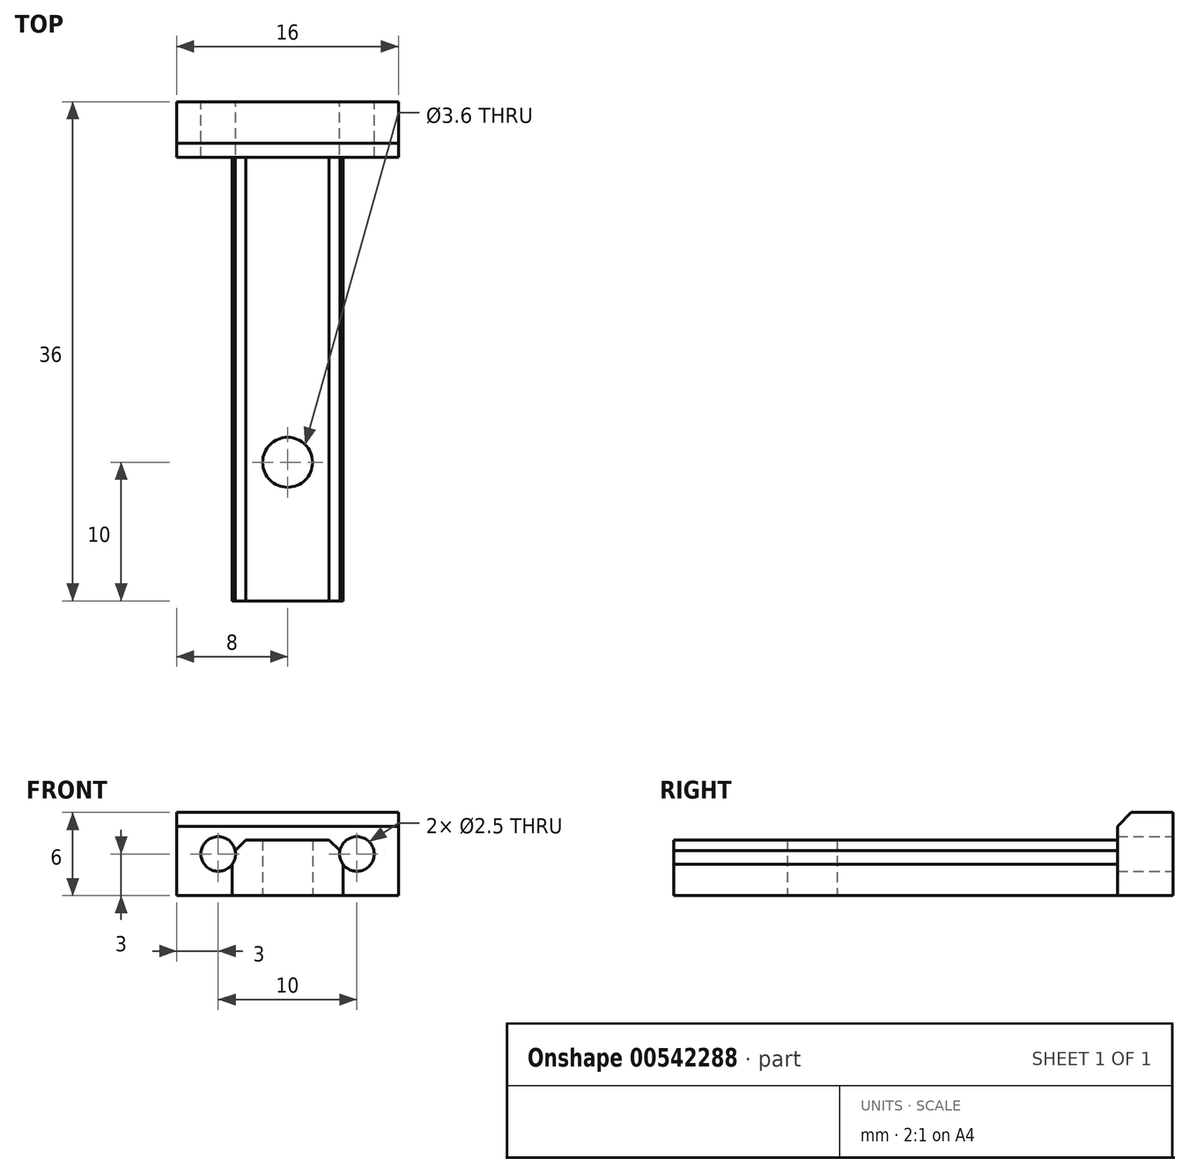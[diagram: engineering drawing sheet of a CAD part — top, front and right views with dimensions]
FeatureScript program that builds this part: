
annotation { "Feature Type Name" : "Feature", "Feature Type Description" : "" }
export const myFeature = defineFeature(function(context is Context, id is Id, definition is map)
    precondition{}
    {
        {
            var Q0;
            Q0=qCreatedBy(makeId("Top.planeOp"),FACE);
            var sketch = newSketch(context, id + "F0", { "sketchPlane" : qUnion([Q0])});
            skLineSegment(sketch, "E0", {"start": v(0, 0) * mm, "end": v(0, 26) * mm, "construction": true});
            skLineSegment(sketch, "E1", {"start": v(0, 0) * mm, "end": v(0, -10) * mm, "construction": true});
            skLineSegment(sketch, "E2", {"start": v(0, 26) * mm, "end": v(-8, 26) * mm});
            skLineSegment(sketch, "E3", {"start": v(0, 26) * mm, "end": v(8, 26) * mm});
            skLineSegment(sketch, "E4", {"start": v(-8, 26) * mm, "end": v(-8, 22) * mm});
            skLineSegment(sketch, "E5", {"start": v(-8, 22) * mm, "end": v(-4, 22) * mm});
            skLineSegment(sketch, "E6", {"start": v(8, 26) * mm, "end": v(8, 22) * mm});
            skLineSegment(sketch, "E7", {"start": v(8, 22) * mm, "end": v(4, 22) * mm});
            skLineSegment(sketch, "E8", {"start": v(0, -10) * mm, "end": v(-4, -10) * mm});
            skLineSegment(sketch, "E9", {"start": v(0, -10) * mm, "end": v(4, -10) * mm});
            skLineSegment(sketch, "E10", {"start": v(-4, 22) * mm, "end": v(-4, -10) * mm});
            skLineSegment(sketch, "E11", {"start": v(4, -10) * mm, "end": v(4, 22) * mm});
            skCircle(sketch, "E12", {"center": v(0, 0) * mm, "radius": 1.8 * mm});
            skLineSegment(sketch, "E13", {"start": v(-4, 22) * mm, "end": v(4, 22) * mm});
            skSolve(sketch);
        }
        {
            var Q0;
            Q0=makeQuery(id+"F0.imprint","IMPRINT",FACE,{"disambiguationData":[TD([[makeQuery(id+"F0.imprint","IMPRINT",EDGE,{"derivedFrom":sQuery(id+"F0.wireOp",EDGE,"E8")}),-1.0]])]});
            extrude(context, id + "F1", {"entities" : qUnion([Q0]), "depth" : 4 * mm, "offsetDistance" : 25 * mm});
        }
        {
            var Q0;
            Q0=makeQuery(id+"F0.imprint","IMPRINT",FACE,{"disambiguationData":[TD([[makeQuery(id+"F0.imprint","IMPRINT",EDGE,{"derivedFrom":sQuery(id+"F0.wireOp",EDGE,"E2")}),1.0]])]});
            extrude(context, id + "F2", {"entities" : qUnion([Q0]), "operationType" : NewBodyOperationType.ADD, "depth" : 6 * mm, "offsetDistance" : 25 * mm});
        }
        {
            var Q0;
            Q0=makeQuery(id+"F2.opExtrude","SWEPT_FACE",FACE,{"disambiguationData":[OSD([sQuery(id+"F0.wireOp",EDGE,"E2"),sQuery(id+"F0.wireOp",EDGE,"E3")])]});
            var sketch = newSketch(context, id + "F3", { "sketchPlane" : qUnion([Q0])});
            skLineSegment(sketch, "E14", {"start": v(0, 3) * mm, "end": v(-5, 3) * mm, "construction": true});
            skPoint(sketch, "E14.startSnap0", {"position": v(8, 3) * mm});
            skLineSegment(sketch, "E15", {"start": v(0, 3) * mm, "end": v(5, 3) * mm, "construction": true});
            skCircle(sketch, "E16", {"center": v(-5, 3) * mm, "radius": 1.25 * mm});
            skCircle(sketch, "E17", {"center": v(5, 3) * mm, "radius": 1.25 * mm});
            skSolve(sketch);
        }
        {
            var Q0;
            Q0=makeQuery(id+"F2.opExtrude","CAP_EDGE",EDGE,{"disambiguationData":[OSD([sQuery(id+"F0.wireOp",EDGE,"E5"),sQuery(id+"F0.wireOp",EDGE,"E7"),sQuery(id+"F0.wireOp",EDGE,"E13")])],"isStart":false});
            var Q1;
            Q1=makeQuery(id+"F1.opExtrude","CAP_EDGE",EDGE,{"disambiguationData":[OSD([sQuery(id+"F0.wireOp",EDGE,"E10")])],"isStart":false});
            var Q2;
            Q2=makeQuery(id+"F1.opExtrude","CAP_EDGE",EDGE,{"disambiguationData":[OSD([sQuery(id+"F0.wireOp",EDGE,"E11")])],"isStart":false});
            chamfer(context, id + "F4", {"entities" : qUnion([Q0, Q1, Q2]), "width" : 1 * mm, "tangentPropagation" : true});
        }
        {
            var Q0;
            Q0=makeQuery(id+"F3.imprint","IMPRINT",FACE,{"disambiguationData":[TD([[makeQuery(id+"F3.imprint","IMPRINT",EDGE,{"derivedFrom":sQuery(id+"F3.wireOp",EDGE,"E16")}),1.0]])]});
            var Q1;
            Q1=makeQuery(id+"F3.imprint","IMPRINT",FACE,{"disambiguationData":[TD([[makeQuery(id+"F3.imprint","IMPRINT",EDGE,{"derivedFrom":sQuery(id+"F3.wireOp",EDGE,"E17")}),1.0]])]});
            extrude(context, id + "F5", {"entities" : qUnion([Q0, Q1]), "operationType" : NewBodyOperationType.REMOVE, "oppositeDirection" : true, "depth" : 40 * mm, "offsetDistance" : 25 * mm});
        }
    });
